# Revit family: Haworth_Swell_PendantOneLight
name_source: partatom
category: Lighting Fixtures
revit_build: Autodesk Revit 2018 (Build: 20170223_1515(x64)
units: mm (PartAtom-declared; Revit-internal decimal feet)

## family parameters
Always vertical = Yes
Cut with Voids When Loaded = No
Light Source = Yes
OmniClass Number = 23.80.70.11.14
OmniClass Title = General Luminaries, Directional
Part Type = Normal
Room Calculation Point = No
Round Connector Dimension = Use Diameter
Shared = No
Work Plane-Based = No

## types (3) — shared parameters
Assembly Code = D5020200
Color Filter = 16777215
Cords Finish = Haworth _ Paint _ Metallic Silver
Dimming Lamp Color Temperature Shift = <None>
Emit Shape Visible in Rendering = No
Emit from Circle Diameter = 24"
Glass Finish = Haworth _ Glass _ Clear
Manufacturer = Haworth
Photometric Web File = generic
Revision Number = 1
Size = Verify Final Dim. w/Haworth
Tilt Angle = 60.00°
URL = http://www.haworth.com
URL - Product = https://www.haworth.com
Warranty = https://www.haworth.com

## per-type parameters (varying)
| type | Actual Depth | Actual Height | Actual Width | Base Radius | Description | Large | Medium | Small | Top Finish |
| LSP1-1610 | 16" | 10" | 16" | 8" | Haworth Swell Pendant with One Light Wide" | Yes | No | No | Haworth _ Paint _ Metallic Silver |
| LSP1-1210 | 12" | 12" | 12" | 6" | Haworth Swell Pendant with One Light Medium" | No | Yes | No | <By Category> |
| LSP1-0810 | 8" | 14" | 8" | 4" | Haworth Swell Pendant with One Light Narrow" | No | No | Yes | <By Category> |

note: column(s) folded — value = type name in every type: Model

## geometry (parser evidence)
native form markers: Sweep x6
no freeform markers — native parametric forms only
